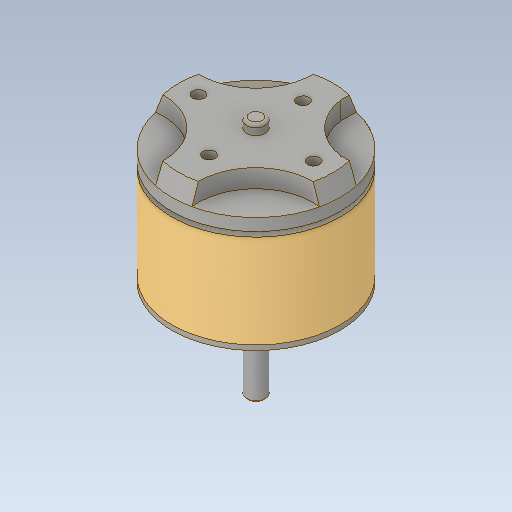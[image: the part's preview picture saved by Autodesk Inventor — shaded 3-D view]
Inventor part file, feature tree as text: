
AUTODESK INVENTOR PART (.ipt)
format: ipt  version: 2020.2 (Build 242310000, 310)  size: 202,752 bytes
history: imported  units: mm
features: imported_body x1
ambient origin geometry x8: Origin, YZ Plane, XZ Plane, XY Plane, X Axis, Y Axis, Z Axis, Center Point
bodies: Solide1 (imported_parasolid), Body2 (imported_parasolid)
feature tree (1):
  imported_body  NMx_Import_Brep_tag  [imported B-rep: ~20 faces, bbox_mm=[26.276184, 5.0, 20.16249]]
